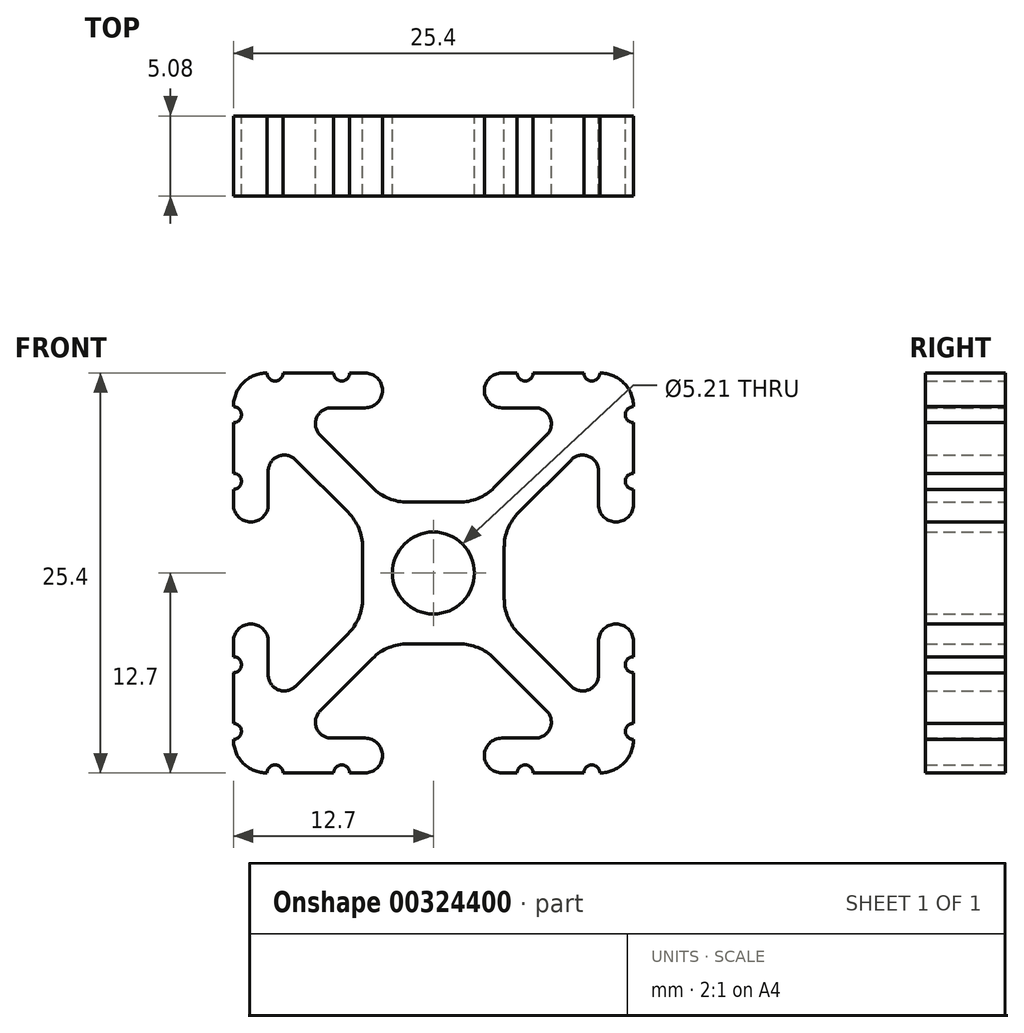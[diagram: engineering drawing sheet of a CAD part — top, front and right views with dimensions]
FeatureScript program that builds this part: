
annotation { "Feature Type Name" : "Feature", "Feature Type Description" : "" }
export const myFeature = defineFeature(function(context is Context, id is Id, definition is map)
    precondition{}
    {
        {
            var Q0;
            Q0=qCreatedBy(makeId("Front.planeOp"),FACE);
            var sketch = newSketch(context, id + "F0", { "sketchPlane" : qUnion([Q0])});
            skArc(sketch, "E0", {"start": v(-12.7, -10.57) * mm, "mid": v(-12.2, -10.06) * mm, "end": v(-12.7, -9.55) * mm});
            skArc(sketch, "E1", {"start": v(-12.7, -10.57) * mm, "mid": v(-12.08, -12.08) * mm, "end": v(-10.57, -12.7) * mm});
            skArc(sketch, "E2", {"start": v(-9.55, -12.7) * mm, "mid": v(-10.06, -12.2) * mm, "end": v(-10.57, -12.7) * mm});
            skLineSegment(sketch, "E3", {"start": v(-9.55, -12.7) * mm, "end": v(-6.33, -12.7) * mm});
            skArc(sketch, "E4", {"start": v(-5.32, -12.7) * mm, "mid": v(-5.83, -12.2) * mm, "end": v(-6.33, -12.7) * mm});
            skLineSegment(sketch, "E5", {"start": v(-5.32, -12.7) * mm, "end": v(-4.34, -12.7) * mm});
            skArc(sketch, "E6", {"start": v(-4.34, -12.7) * mm, "mid": v(-3.24, -11.6) * mm, "end": v(-4.34, -10.5) * mm});
            skLineSegment(sketch, "E7", {"start": v(-4.34, -10.5) * mm, "end": v(-6.47, -10.5) * mm});
            skArc(sketch, "E8", {"start": v(-7.2, -8.76) * mm, "mid": v(-7.41, -9.86) * mm, "end": v(-6.47, -10.5) * mm});
            skLineSegment(sketch, "E9", {"start": v(-7.2, -8.76) * mm, "end": v(-3.86, -5.43) * mm});
            skArc(sketch, "E10", {"start": v(-1.62, -4.5) * mm, "mid": v(-2.83, -4.74) * mm, "end": v(-3.86, -5.43) * mm});
            skLineSegment(sketch, "E11", {"start": v(-1.62, -4.5) * mm, "end": v(1.62, -4.5) * mm});
            skArc(sketch, "E12", {"start": v(3.86, -5.43) * mm, "mid": v(2.83, -4.74) * mm, "end": v(1.62, -4.5) * mm});
            skLineSegment(sketch, "E13", {"start": v(3.86, -5.43) * mm, "end": v(7.2, -8.76) * mm});
            skArc(sketch, "E14", {"start": v(6.47, -10.5) * mm, "mid": v(7.41, -9.86) * mm, "end": v(7.2, -8.76) * mm});
            skLineSegment(sketch, "E15", {"start": v(6.47, -10.5) * mm, "end": v(4.34, -10.5) * mm});
            skArc(sketch, "E16", {"start": v(4.34, -10.5) * mm, "mid": v(3.24, -11.6) * mm, "end": v(4.34, -12.7) * mm});
            skLineSegment(sketch, "E17", {"start": v(4.34, -12.7) * mm, "end": v(5.32, -12.7) * mm});
            skArc(sketch, "E18", {"start": v(6.33, -12.7) * mm, "mid": v(5.83, -12.2) * mm, "end": v(5.32, -12.7) * mm});
            skLineSegment(sketch, "E19", {"start": v(6.33, -12.7) * mm, "end": v(9.55, -12.7) * mm});
            skArc(sketch, "E20", {"start": v(10.57, -12.7) * mm, "mid": v(10.06, -12.2) * mm, "end": v(9.55, -12.7) * mm});
            skArc(sketch, "E21", {"start": v(10.57, -12.7) * mm, "mid": v(12.08, -12.08) * mm, "end": v(12.7, -10.57) * mm});
            skArc(sketch, "E22", {"start": v(12.7, -9.55) * mm, "mid": v(12.2, -10.06) * mm, "end": v(12.7, -10.57) * mm});
            skLineSegment(sketch, "E23", {"start": v(12.7, -9.55) * mm, "end": v(12.7, -6.33) * mm});
            skArc(sketch, "E24", {"start": v(12.7, -5.32) * mm, "mid": v(12.2, -5.83) * mm, "end": v(12.7, -6.33) * mm});
            skLineSegment(sketch, "E25", {"start": v(12.7, -5.32) * mm, "end": v(12.7, -4.34) * mm});
            skArc(sketch, "E26", {"start": v(12.7, -4.34) * mm, "mid": v(11.6, -3.24) * mm, "end": v(10.5, -4.34) * mm});
            skLineSegment(sketch, "E27", {"start": v(10.5, -4.34) * mm, "end": v(10.5, -6.47) * mm});
            skArc(sketch, "E28", {"start": v(8.76, -7.2) * mm, "mid": v(9.86, -7.41) * mm, "end": v(10.5, -6.47) * mm});
            skLineSegment(sketch, "E29", {"start": v(8.76, -7.2) * mm, "end": v(5.43, -3.86) * mm});
            skArc(sketch, "E30", {"start": v(4.5, -1.62) * mm, "mid": v(4.74, -2.83) * mm, "end": v(5.43, -3.86) * mm});
            skLineSegment(sketch, "E31", {"start": v(4.5, -1.62) * mm, "end": v(4.5, 1.62) * mm});
            skArc(sketch, "E32", {"start": v(5.43, 3.86) * mm, "mid": v(4.74, 2.83) * mm, "end": v(4.5, 1.62) * mm});
            skLineSegment(sketch, "E33", {"start": v(5.43, 3.86) * mm, "end": v(8.76, 7.2) * mm});
            skArc(sketch, "E34", {"start": v(10.5, 6.47) * mm, "mid": v(9.86, 7.41) * mm, "end": v(8.76, 7.2) * mm});
            skLineSegment(sketch, "E35", {"start": v(10.5, 6.47) * mm, "end": v(10.5, 4.34) * mm});
            skArc(sketch, "E36", {"start": v(10.5, 4.34) * mm, "mid": v(11.6, 3.24) * mm, "end": v(12.7, 4.34) * mm});
            skLineSegment(sketch, "E37", {"start": v(12.7, 4.34) * mm, "end": v(12.7, 5.32) * mm});
            skArc(sketch, "E38", {"start": v(12.7, 6.33) * mm, "mid": v(12.2, 5.83) * mm, "end": v(12.7, 5.32) * mm});
            skLineSegment(sketch, "E39", {"start": v(12.7, 6.33) * mm, "end": v(12.7, 9.55) * mm});
            skArc(sketch, "E40", {"start": v(12.7, 10.57) * mm, "mid": v(12.2, 10.06) * mm, "end": v(12.7, 9.55) * mm});
            skArc(sketch, "E41", {"start": v(12.7, 10.57) * mm, "mid": v(12.08, 12.08) * mm, "end": v(10.57, 12.7) * mm});
            skArc(sketch, "E42", {"start": v(9.55, 12.7) * mm, "mid": v(10.06, 12.2) * mm, "end": v(10.57, 12.7) * mm});
            skLineSegment(sketch, "E43", {"start": v(9.55, 12.7) * mm, "end": v(6.33, 12.7) * mm});
            skArc(sketch, "E44", {"start": v(5.32, 12.7) * mm, "mid": v(5.83, 12.2) * mm, "end": v(6.33, 12.7) * mm});
            skLineSegment(sketch, "E45", {"start": v(5.32, 12.7) * mm, "end": v(4.34, 12.7) * mm});
            skArc(sketch, "E46", {"start": v(4.34, 12.7) * mm, "mid": v(3.24, 11.6) * mm, "end": v(4.34, 10.5) * mm});
            skLineSegment(sketch, "E47", {"start": v(4.34, 10.5) * mm, "end": v(6.47, 10.5) * mm});
            skArc(sketch, "E48", {"start": v(7.2, 8.76) * mm, "mid": v(7.41, 9.86) * mm, "end": v(6.47, 10.5) * mm});
            skLineSegment(sketch, "E49", {"start": v(7.2, 8.76) * mm, "end": v(3.86, 5.43) * mm});
            skArc(sketch, "E50", {"start": v(1.62, 4.5) * mm, "mid": v(2.83, 4.74) * mm, "end": v(3.86, 5.43) * mm});
            skLineSegment(sketch, "E51", {"start": v(1.62, 4.5) * mm, "end": v(-1.62, 4.5) * mm});
            skArc(sketch, "E52", {"start": v(-3.86, 5.43) * mm, "mid": v(-2.83, 4.74) * mm, "end": v(-1.62, 4.5) * mm});
            skLineSegment(sketch, "E53", {"start": v(-3.86, 5.43) * mm, "end": v(-7.2, 8.76) * mm});
            skArc(sketch, "E54", {"start": v(-6.47, 10.5) * mm, "mid": v(-7.41, 9.86) * mm, "end": v(-7.2, 8.76) * mm});
            skLineSegment(sketch, "E55", {"start": v(-6.47, 10.5) * mm, "end": v(-4.34, 10.5) * mm});
            skArc(sketch, "E56", {"start": v(-4.34, 10.5) * mm, "mid": v(-3.24, 11.6) * mm, "end": v(-4.34, 12.7) * mm});
            skLineSegment(sketch, "E57", {"start": v(-4.34, 12.7) * mm, "end": v(-5.32, 12.7) * mm});
            skArc(sketch, "E58", {"start": v(-6.33, 12.7) * mm, "mid": v(-5.83, 12.2) * mm, "end": v(-5.32, 12.7) * mm});
            skLineSegment(sketch, "E59", {"start": v(-6.33, 12.7) * mm, "end": v(-9.55, 12.7) * mm});
            skArc(sketch, "E60", {"start": v(-10.57, 12.7) * mm, "mid": v(-10.06, 12.2) * mm, "end": v(-9.55, 12.7) * mm});
            skArc(sketch, "E61", {"start": v(-10.57, 12.7) * mm, "mid": v(-12.08, 12.08) * mm, "end": v(-12.7, 10.57) * mm});
            skArc(sketch, "E62", {"start": v(-12.7, 9.55) * mm, "mid": v(-12.2, 10.06) * mm, "end": v(-12.7, 10.57) * mm});
            skLineSegment(sketch, "E63", {"start": v(-12.7, 9.55) * mm, "end": v(-12.7, 6.33) * mm});
            skArc(sketch, "E64", {"start": v(-12.7, 5.32) * mm, "mid": v(-12.2, 5.83) * mm, "end": v(-12.7, 6.33) * mm});
            skLineSegment(sketch, "E65", {"start": v(-12.7, 5.32) * mm, "end": v(-12.7, 4.34) * mm});
            skArc(sketch, "E66", {"start": v(-12.7, 4.34) * mm, "mid": v(-11.6, 3.24) * mm, "end": v(-10.5, 4.34) * mm});
            skLineSegment(sketch, "E67", {"start": v(-10.5, 4.34) * mm, "end": v(-10.5, 6.47) * mm});
            skArc(sketch, "E68", {"start": v(-8.76, 7.2) * mm, "mid": v(-9.86, 7.41) * mm, "end": v(-10.5, 6.47) * mm});
            skLineSegment(sketch, "E69", {"start": v(-8.76, 7.2) * mm, "end": v(-5.43, 3.86) * mm});
            skArc(sketch, "E70", {"start": v(-4.5, 1.62) * mm, "mid": v(-4.74, 2.83) * mm, "end": v(-5.43, 3.86) * mm});
            skLineSegment(sketch, "E71", {"start": v(-4.5, 1.62) * mm, "end": v(-4.5, -1.62) * mm});
            skArc(sketch, "E72", {"start": v(-5.43, -3.86) * mm, "mid": v(-4.74, -2.83) * mm, "end": v(-4.5, -1.62) * mm});
            skLineSegment(sketch, "E73", {"start": v(-5.43, -3.86) * mm, "end": v(-8.76, -7.2) * mm});
            skArc(sketch, "E74", {"start": v(-10.5, -6.47) * mm, "mid": v(-9.86, -7.41) * mm, "end": v(-8.76, -7.2) * mm});
            skLineSegment(sketch, "E75", {"start": v(-10.5, -6.47) * mm, "end": v(-10.5, -4.34) * mm});
            skArc(sketch, "E76", {"start": v(-10.5, -4.34) * mm, "mid": v(-11.6, -3.24) * mm, "end": v(-12.7, -4.34) * mm});
            skLineSegment(sketch, "E77", {"start": v(-12.7, -4.34) * mm, "end": v(-12.7, -5.32) * mm});
            skArc(sketch, "E78", {"start": v(-12.7, -6.33) * mm, "mid": v(-12.2, -5.83) * mm, "end": v(-12.7, -5.32) * mm});
            skLineSegment(sketch, "E79", {"start": v(-12.7, -6.33) * mm, "end": v(-12.7, -9.55) * mm});
            skArc(sketch, "E80", {"start": v(2.6, 0) * mm, "mid": v(0, 2.6) * mm, "end": v(-2.6, 0) * mm});
            skArc(sketch, "E81", {"start": v(-2.6, 0) * mm, "mid": v(0, -2.6) * mm, "end": v(2.6, 0) * mm});
            skSolve(sketch);
        }
        {
            var Q0;
            Q0=makeQuery(id+"F0.imprint","IMPRINT",FACE,{"disambiguationData":[TD([[makeQuery(id+"F0.imprint","IMPRINT",EDGE,{"derivedFrom":sQuery(id+"F0.wireOp",EDGE,"E0")}),-1.0]])]});
            extrude(context, id + "F1", {"entities" : qUnion([Q0]), "depth" : 5.08 * mm});
        }
    });
